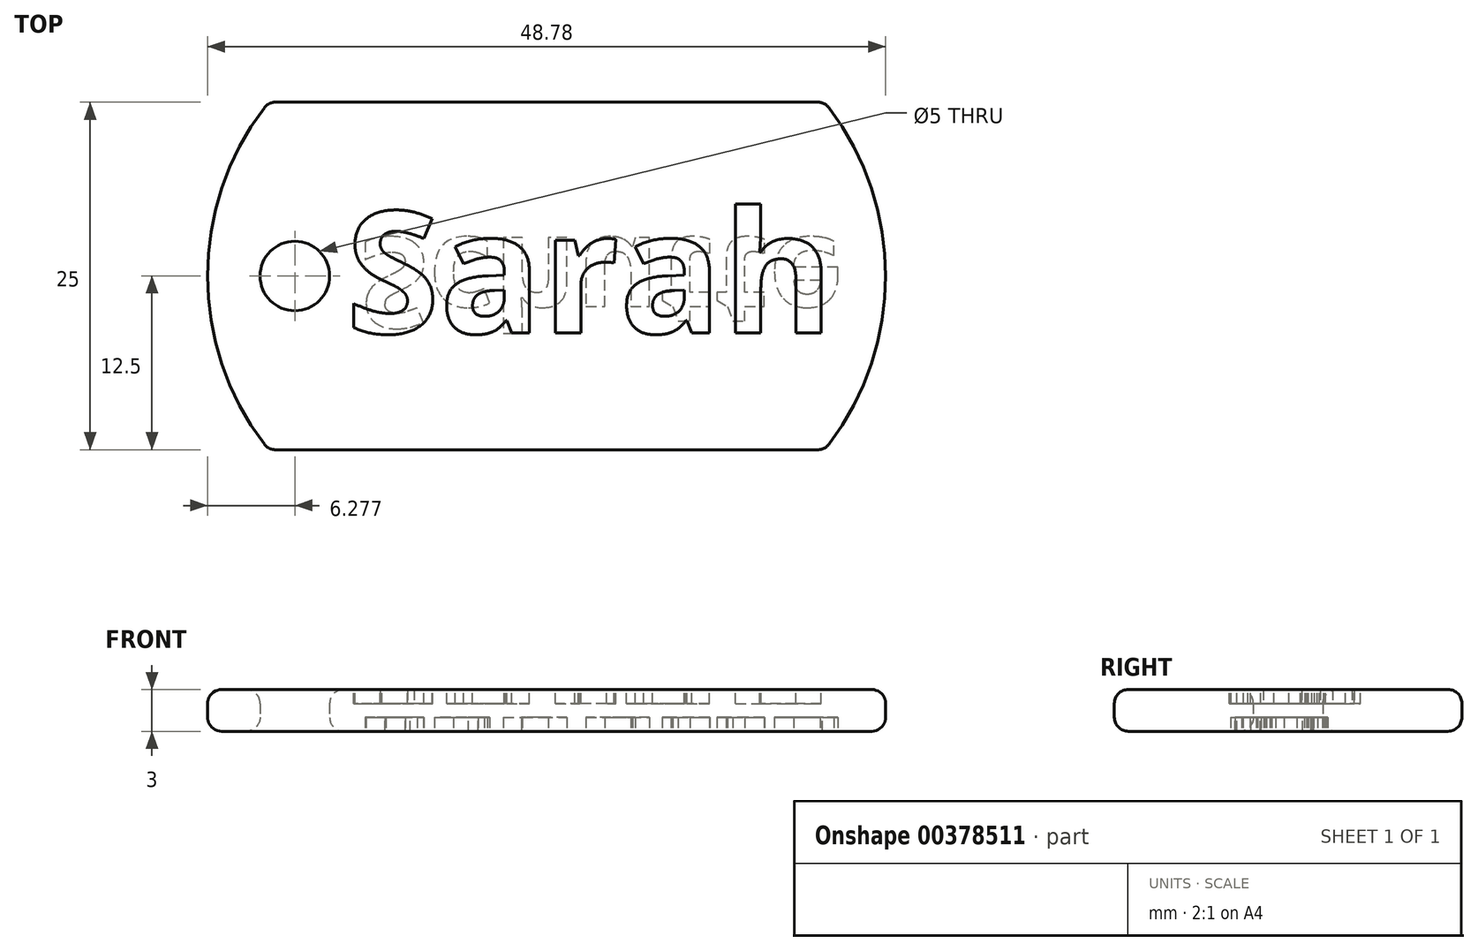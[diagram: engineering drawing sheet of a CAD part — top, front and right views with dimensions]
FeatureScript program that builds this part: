
annotation { "Feature Type Name" : "Feature", "Feature Type Description" : "" }
export const myFeature = defineFeature(function(context is Context, id is Id, definition is map)
    precondition{}
    {
        {
            var Q0;
            Q0=qCreatedBy(makeId("Top.planeOp"),FACE);
            var sketch = newSketch(context, id + "F0", { "sketchPlane" : qUnion([Q0])});
            skLineSegment(sketch, "E0.bottom", {"start": v(-20, 12.5) * mm, "end": v(20, 12.5) * mm});
            skLineSegment(sketch, "E0.top", {"start": v(-20, -12.5) * mm, "end": v(20, -12.5) * mm});
            skArc(sketch, "E1", {"start": v(-20, 12.5) * mm, "mid": v(-24.39, 0) * mm, "end": v(-20, -12.5) * mm});
            skArc(sketch, "E2", {"start": v(20, -12.5) * mm, "mid": v(24.39, 0) * mm, "end": v(20, 12.5) * mm});
            skCircle(sketch, "E3", {"center": v(-18.11, 0) * mm, "radius": 2.5 * mm});
            skSolve(sketch);
        }
        {
            var Q0;
            Q0=makeQuery(id+"F0.imprint","IMPRINT",FACE,{"disambiguationData":[TD([[makeQuery(id+"F0.imprint","IMPRINT",EDGE,{"derivedFrom":sQuery(id+"F0.wireOp",EDGE,"E0.bottom")}),-1.0]])]});
            extrude(context, id + "F1", {"entities" : qUnion([Q0]), "depth" : 3 * mm});
        }
        {
            var Q0;
            Q0=makeQuery(id+"F1.opExtrude","CAP_FACE",FACE,{"disambiguationData":[OSD([sQuery(id+"F0.wireOp",EDGE,"E0.bottom"),sQuery(id+"F0.wireOp",EDGE,"E0.top"),sQuery(id+"F0.wireOp",EDGE,"E1"),sQuery(id+"F0.wireOp",EDGE,"E2"),sQuery(id+"F0.wireOp",EDGE,"E3")])],"isStart":false});
            var sketch = newSketch(context, id + "F2", { "sketchPlane" : qUnion([Q0])});
            skText(sketch, "E4", { "text": "Sarah", "fontName": "OpenSans-Bold.ttf"});
            const initialGuessF2  = {"E4": [-0.01445, -0.00411, 1, 0, 0.00881]};
            skSetInitialGuess(sketch, initialGuessF2);
            skSolve(sketch);
        }
        {
            var Q0;
            Q0=qSketchRegion(id+"F2",true);
            extrude(context, id + "F3", {"entities" : qUnion([Q0]), "operationType" : NewBodyOperationType.REMOVE, "oppositeDirection" : true, "depth" : 1 * mm});
        }
        {
            var Q0;
            Q0=makeQuery(id+"F1.opExtrude","CAP_FACE",FACE,{"disambiguationData":[OSD([sQuery(id+"F0.wireOp",EDGE,"E0.bottom"),sQuery(id+"F0.wireOp",EDGE,"E0.top"),sQuery(id+"F0.wireOp",EDGE,"E1"),sQuery(id+"F0.wireOp",EDGE,"E2"),sQuery(id+"F0.wireOp",EDGE,"E3")])],"isStart":true});
            var sketch = newSketch(context, id + "F4", { "sketchPlane" : qUnion([Q0])});
            skText(sketch, "E5", { "text": "Schutte", "fontName": "OpenSans-Bold.ttf"});
            const initialGuessF4  = {"E5": [-0.01347, -0.00276, 1, 0, 0.00653]};
            skSetInitialGuess(sketch, initialGuessF4);
            skSolve(sketch);
        }
        {
            var Q0;
            Q0=qSketchRegion(id+"F4",true);
            extrude(context, id + "F5", {"entities" : qUnion([Q0]), "operationType" : NewBodyOperationType.REMOVE, "oppositeDirection" : true, "depth" : 1 * mm});
        }
        {
            var Q0;
            Q0=makeQuery(id+"F1.opExtrude","SWEPT_FACE",FACE,{"disambiguationData":[OSD([sQuery(id+"F0.wireOp",EDGE,"E2")])]});
            var Q1;
            Q1=makeQuery(id+"F1.opExtrude","SWEPT_FACE",FACE,{"disambiguationData":[OSD([sQuery(id+"F0.wireOp",EDGE,"E0.top")])]});
            var Q2;
            Q2=makeQuery(id+"F1.opExtrude","SWEPT_FACE",FACE,{"disambiguationData":[OSD([sQuery(id+"F0.wireOp",EDGE,"E3")])]});
            var Q3;
            Q3=makeQuery(id+"F1.opExtrude","SWEPT_FACE",FACE,{"disambiguationData":[OSD([sQuery(id+"F0.wireOp",EDGE,"E1")])]});
            var Q4;
            Q4=makeQuery(id+"F1.opExtrude","SWEPT_FACE",FACE,{"disambiguationData":[OSD([sQuery(id+"F0.wireOp",EDGE,"E0.bottom")])]});
            fillet(context, id + "F6", {"entities" : qUnion([Q0, Q1, Q2, Q3, Q4]), "radius" : 1 * mm, "tangentPropagation" : true, "allowEdgeOverflow" : false});
        }
    });
